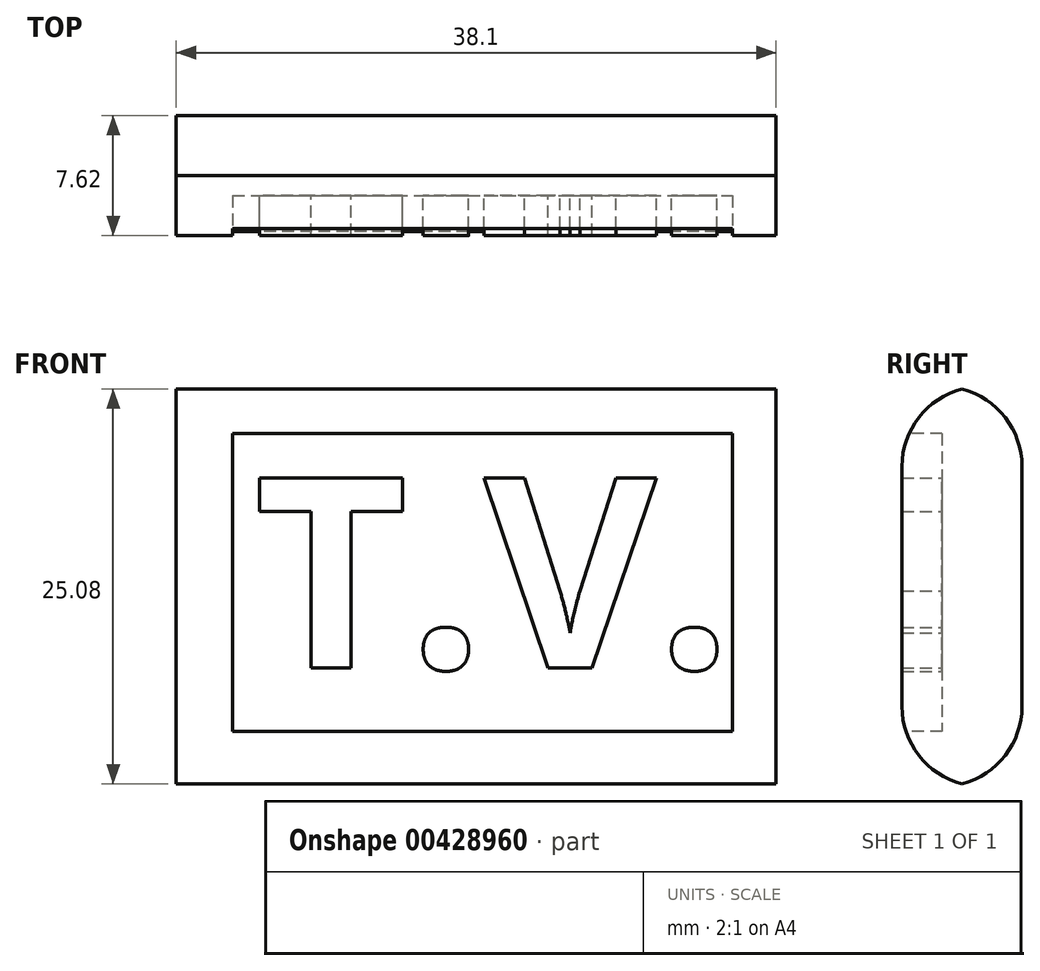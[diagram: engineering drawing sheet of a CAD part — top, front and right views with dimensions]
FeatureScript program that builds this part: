
annotation { "Feature Type Name" : "Feature", "Feature Type Description" : "" }
export const myFeature = defineFeature(function(context is Context, id is Id, definition is map)
    precondition{}
    {
        {
            var Q0;
            Q0=qCreatedBy(makeId("Front.planeOp"),FACE);
            var sketch = newSketch(context, id + "F0", { "sketchPlane" : qUnion([Q0])});
            skLineSegment(sketch, "E0.bottom", {"start": v(0, 0) * mm, "end": v(38.1, 0) * mm});
            skLineSegment(sketch, "E0.top", {"start": v(0, -25.4) * mm, "end": v(38.1, -25.4) * mm});
            skLineSegment(sketch, "E0.left", {"start": v(0, 0) * mm, "end": v(0, -25.4) * mm});
            skLineSegment(sketch, "E0.right", {"start": v(38.1, 0) * mm, "end": v(38.1, -25.4) * mm});
            skSolve(sketch);
        }
        {
            var Q0;
            Q0 = qSketchRegion(id + "F0", true);
            extrude(context, id + "F1", {"entities" : qUnion([Q0]), "depth" : 7.62 * mm});
        }
        {
            var Q0;
            Q0=makeQuery(id+"F1.opExtrude","CAP_FACE",FACE,{"disambiguationData":[OSD([sQuery(id+"F0.wireOp",EDGE,"E0.bottom"),sQuery(id+"F0.wireOp",EDGE,"E0.top"),sQuery(id+"F0.wireOp",EDGE,"E0.left"),sQuery(id+"F0.wireOp",EDGE,"E0.right")])],"isStart":false});
            var sketch = newSketch(context, id + "F2", { "sketchPlane" : qUnion([Q0])});
            skLineSegment(sketch, "E1.bottom", {"start": v(3.59, -2.98) * mm, "end": v(35.34, -2.98) * mm});
            skLineSegment(sketch, "E1.top", {"start": v(3.59, -21.92) * mm, "end": v(35.34, -21.92) * mm});
            skLineSegment(sketch, "E1.left", {"start": v(3.59, -2.98) * mm, "end": v(3.59, -21.92) * mm});
            skLineSegment(sketch, "E1.right", {"start": v(35.34, -2.98) * mm, "end": v(35.34, -21.92) * mm});
            skSolve(sketch);
        }
        {
            var Q0;
            Q0 = qSketchRegion(id + "F2", true);
            extrude(context, id + "F3", {"entities" : qUnion([Q0]), "operationType" : NewBodyOperationType.REMOVE, "oppositeDirection" : true, "depth" : 2.54 * mm});
        }
        {
            var Q0;
            Q0=makeQuery(id+"F1.opExtrude","CAP_EDGE",EDGE,{"disambiguationData":[OSD([sQuery(id+"F0.wireOp",EDGE,"E0.bottom")])],"isStart":false});
            var Q1;
            Q1=makeQuery(id+"F1.opExtrude","CAP_EDGE",EDGE,{"disambiguationData":[OSD([sQuery(id+"F0.wireOp",EDGE,"E0.bottom")])],"isStart":true});
            var Q2;
            Q2=makeQuery(id+"F1.opExtrude","CAP_EDGE",EDGE,{"disambiguationData":[OSD([sQuery(id+"F0.wireOp",EDGE,"E0.top")])],"isStart":false});
            var Q3;
            Q3=makeQuery(id+"F1.opExtrude","CAP_EDGE",EDGE,{"disambiguationData":[OSD([sQuery(id+"F0.wireOp",EDGE,"E0.top")])],"isStart":true});
            fillet(context, id + "F4", {"entities" : qUnion([Q0, Q1, Q2, Q3]), "radius" : 5.08 * mm, "tangentPropagation" : true, "allowEdgeOverflow" : false});
        }
        {
            var Q0;
            Q0=makeQuery(id+"F3.boolean.opBoolean","COPY",FACE,{"derivedFrom":makeQuery(id+"F3.opExtrude","CAP_FACE",FACE,{"disambiguationData":[OSD([sQuery(id+"F2.wireOp",EDGE,"E1.bottom"),sQuery(id+"F2.wireOp",EDGE,"E1.top"),sQuery(id+"F2.wireOp",EDGE,"E1.left"),sQuery(id+"F2.wireOp",EDGE,"E1.right")])],"isStart":false})});
            var sketch = newSketch(context, id + "F5", { "sketchPlane" : qUnion([Q0])});
            skText(sketch, "E2", { "text": "T.V.", "fontName": "OpenSans-Bold.ttf"});
            const initialGuessF5  = {"E2": [0.00495, -0.01787, 1, 0, 0.01215]};
            skSetInitialGuess(sketch, initialGuessF5);
            skSolve(sketch);
        }
        {
            var Q0;
            Q0 = qSketchRegion(id + "F5", true);
            extrude(context, id + "F6", {"entities" : qUnion([Q0]), "operationType" : NewBodyOperationType.ADD, "depth" : 2.54 * mm});
        }
    });
